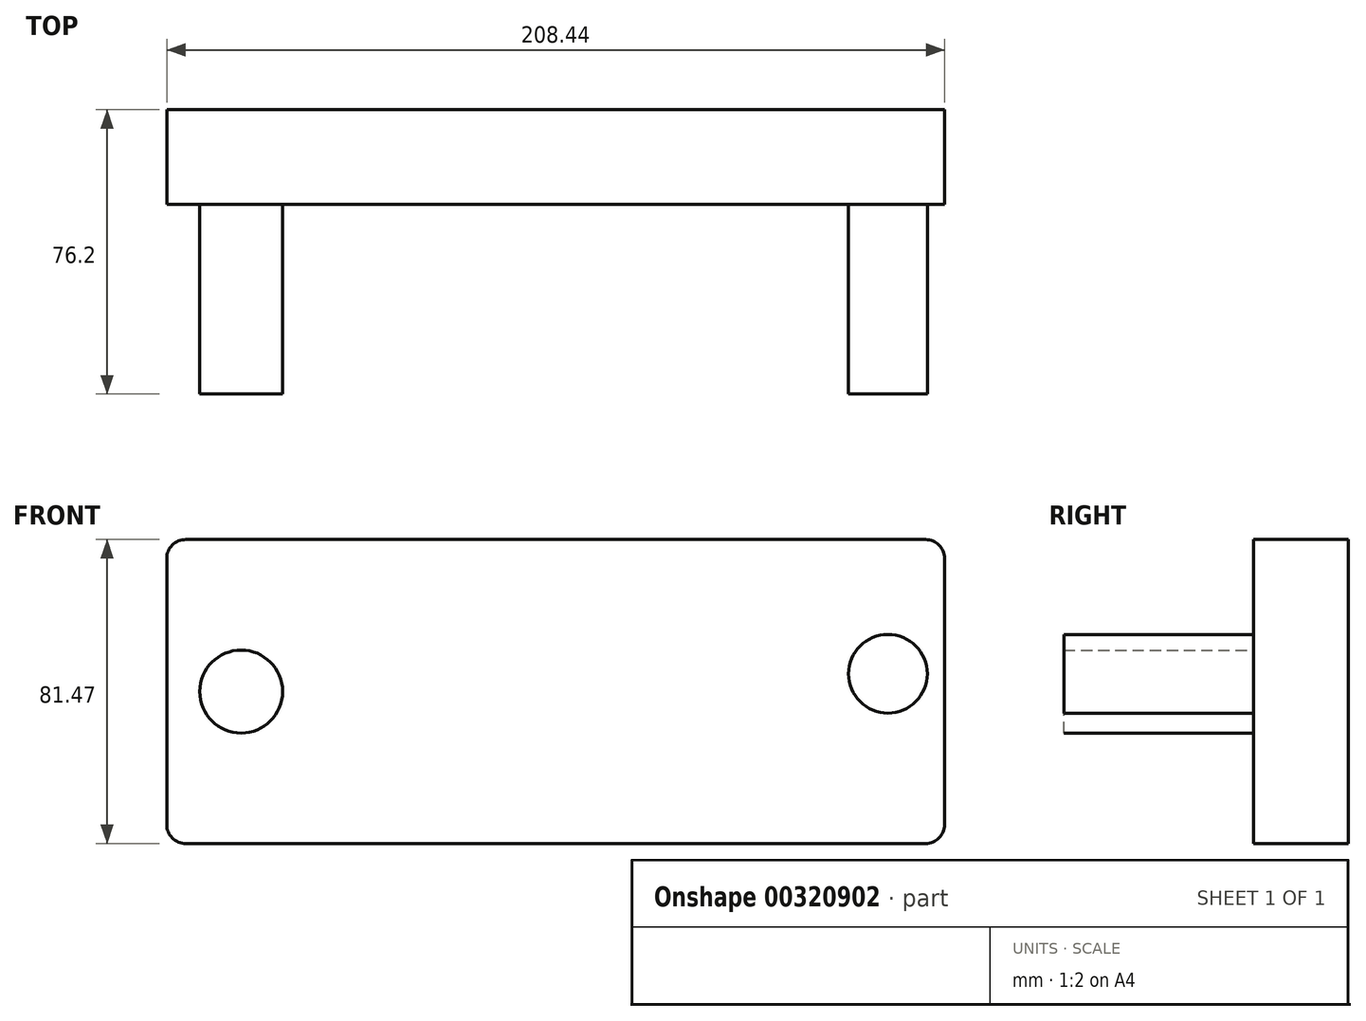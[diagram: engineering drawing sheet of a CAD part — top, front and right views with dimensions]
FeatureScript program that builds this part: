
annotation { "Feature Type Name" : "Feature", "Feature Type Description" : "" }
export const myFeature = defineFeature(function(context is Context, id is Id, definition is map)
    precondition{}
    {
        {
            var Q0;
            Q0=qCreatedBy(makeId("Front.planeOp"),FACE);
            var sketch = newSketch(context, id + "F0", { "sketchPlane" : qUnion([Q0])});
            skLineSegment(sketch, "E0.bottom", {"start": v(-108.12, 35.97) * mm, "end": v(100.32, 35.97) * mm});
            skLineSegment(sketch, "E0.top", {"start": v(-108.12, -45.5) * mm, "end": v(100.32, -45.5) * mm});
            skLineSegment(sketch, "E0.left", {"start": v(-108.12, 35.97) * mm, "end": v(-108.12, -45.5) * mm});
            skLineSegment(sketch, "E0.right", {"start": v(100.32, 35.97) * mm, "end": v(100.32, -45.5) * mm});
            skSolve(sketch);
        }
        {
            var Q0;
            Q0 = qSketchRegion(id + "F0", true);
            extrude(context, id + "F1", {"entities" : qUnion([Q0]), "depth" : 25.4 * mm});
        }
        {
            var Q0;
            Q0=makeQuery(id+"F1.opExtrude","CAP_FACE",FACE,{"disambiguationData":[OSD([sQuery(id+"F0.wireOp",EDGE,"E0.bottom"),sQuery(id+"F0.wireOp",EDGE,"E0.top"),sQuery(id+"F0.wireOp",EDGE,"E0.left"),sQuery(id+"F0.wireOp",EDGE,"E0.right")])],"isStart":false});
            var sketch = newSketch(context, id + "F2", { "sketchPlane" : qUnion([Q0])});
            skCircle(sketch, "E1", {"center": v(-88.19, -4.77) * mm, "radius": 11.1 * mm});
            skCircle(sketch, "E2", {"center": v(85.15, 0) * mm, "radius": 10.54 * mm});
            skSolve(sketch);
        }
        {
            var Q0;
            Q0 = qSketchRegion(id + "F2", true);
            extrude(context, id + "F3", {"entities" : qUnion([Q0]), "operationType" : NewBodyOperationType.ADD, "depth" : 50.8 * mm});
        }
        {
            var Q0;
            Q0=makeQuery(id+"F1.opExtrude","CAP_FACE",FACE,{"disambiguationData":[OSD([sQuery(id+"F0.wireOp",EDGE,"E0.bottom"),sQuery(id+"F0.wireOp",EDGE,"E0.top"),sQuery(id+"F0.wireOp",EDGE,"E0.left"),sQuery(id+"F0.wireOp",EDGE,"E0.right")])],"isStart":true});
            var sketch = newSketch(context, id + "F4", { "sketchPlane" : qUnion([Q0])});
            skSolve(sketch);
        }
        {
            var Q0;
            Q0=makeQuery(id+"F1.opExtrude","CAP_FACE",FACE,{"disambiguationData":[OSD([sQuery(id+"F0.wireOp",EDGE,"E0.bottom"),sQuery(id+"F0.wireOp",EDGE,"E0.top"),sQuery(id+"F0.wireOp",EDGE,"E0.left"),sQuery(id+"F0.wireOp",EDGE,"E0.right")])],"isStart":false});
            var sketch = newSketch(context, id + "F5", { "sketchPlane" : qUnion([Q0])});
            skCircle(sketch, "E3", {"center": v(0, 0) * mm, "radius": 18.38 * mm});
            skSolve(sketch);
        }
        {
            var Q0;
            Q0=sQuery(id+"F5.wireOp",EDGE,"E3");
            extrude(context, id + "F6", {"bodyType" : ToolBodyType.SURFACE, "surfaceEntities" : qUnion([Q0]), "depth" : 50.8 * mm});
        }
        {
            var Q0;
            Q0=makeQuery(id+"F1.opExtrude","SWEPT_EDGE",EDGE,{"disambiguationData":[OSD([sQuery(id+"F0.wireOp",EDGE,"E0.top"),sQuery(id+"F0.wireOp",EDGE,"E0.right")])]});
            var Q1;
            Q1=makeQuery(id+"F1.opExtrude","SWEPT_EDGE",EDGE,{"disambiguationData":[OSD([sQuery(id+"F0.wireOp",EDGE,"E0.top"),sQuery(id+"F0.wireOp",EDGE,"E0.left")])]});
            var Q2;
            Q2=makeQuery(id+"F1.opExtrude","SWEPT_EDGE",EDGE,{"disambiguationData":[OSD([sQuery(id+"F0.wireOp",EDGE,"E0.bottom"),sQuery(id+"F0.wireOp",EDGE,"E0.left")])]});
            var Q3;
            Q3=makeQuery(id+"F1.opExtrude","SWEPT_EDGE",EDGE,{"disambiguationData":[OSD([sQuery(id+"F0.wireOp",EDGE,"E0.bottom"),sQuery(id+"F0.wireOp",EDGE,"E0.right")])]});
            fillet(context, id + "F7", {"entities" : qUnion([Q0, Q1, Q2, Q3]), "radius" : 5.08 * mm, "tangentPropagation" : true, "allowEdgeOverflow" : false});
        }
        {
            var Q0;
            Q0=makeQuery(id+"F4.imprint","IMPRINT",FACE,{"disambiguationData":[TD([[makeQuery(id+"F4.imprint","IMPRINT",EDGE,{"derivedFrom":makeQuery(id+"F1.opExtrude","CAP_EDGE",EDGE,{"disambiguationData":[OSD([sQuery(id+"F0.wireOp",EDGE,"E0.bottom")])],"isStart":true})}),1.0]])]});
            var sketch = newSketch(context, id + "F8", { "sketchPlane" : qUnion([Q0])});
            skArc(sketch, "E4", {"start": v(-90.5, -15.2) * mm, "mid": v(1, -36.5) * mm, "end": v(93.07, -17.86) * mm});
            skSolve(sketch);
        }
        {
            var Q0;
            Q0=sQuery(id+"F8.wireOp",EDGE,"E4");
            extrude(context, id + "F9", {"bodyType" : ToolBodyType.SURFACE, "surfaceEntities" : qUnion([Q0]), "depth" : 25.4 * mm});
        }
    });
